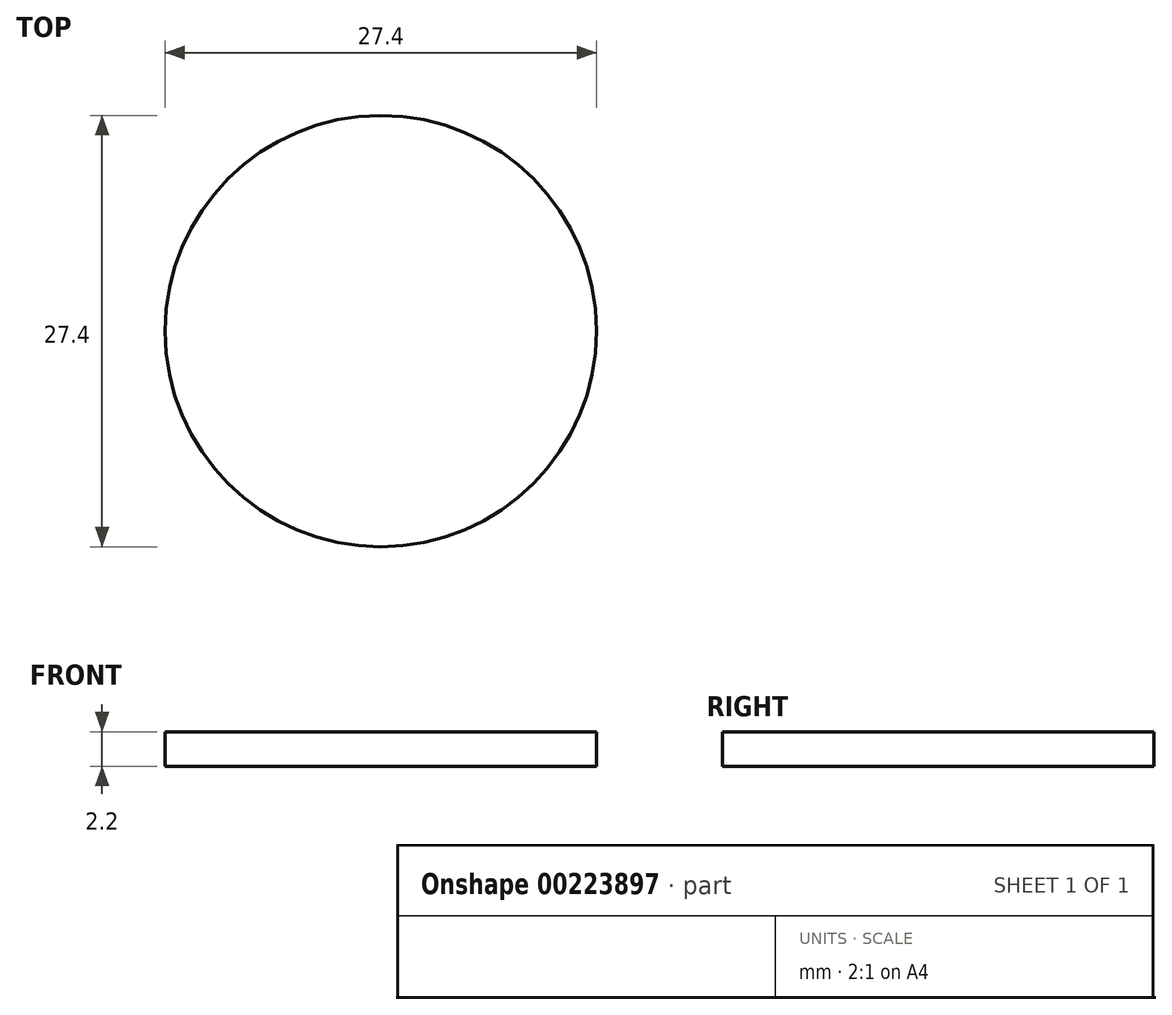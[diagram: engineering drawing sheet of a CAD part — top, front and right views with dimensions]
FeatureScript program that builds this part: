
annotation { "Feature Type Name" : "Feature", "Feature Type Description" : "" }
export const myFeature = defineFeature(function(context is Context, id is Id, definition is map)
    precondition{}
    {
        {
            var Q0;
            Q0=qCreatedBy(makeId("Top.planeOp"),FACE);
            var sketch = newSketch(context, id + "F0", { "sketchPlane" : qUnion([Q0])});
            skCircle(sketch, "E0", {"center": v(0, 0) * mm, "radius": 13.7 * mm});
            skSolve(sketch);
        }
        {
            var Q0;
            Q0=makeQuery(id+"F0.imprint","IMPRINT",FACE,{"disambiguationData":[TD([[makeQuery(id+"F0.imprint","IMPRINT",EDGE,{"derivedFrom":sQuery(id+"F0.wireOp",EDGE,"E0")}),1.0]])]});
            extrude(context, id + "F1", {"entities" : qUnion([Q0]), "depth" : 2.2 * mm});
        }
    });
